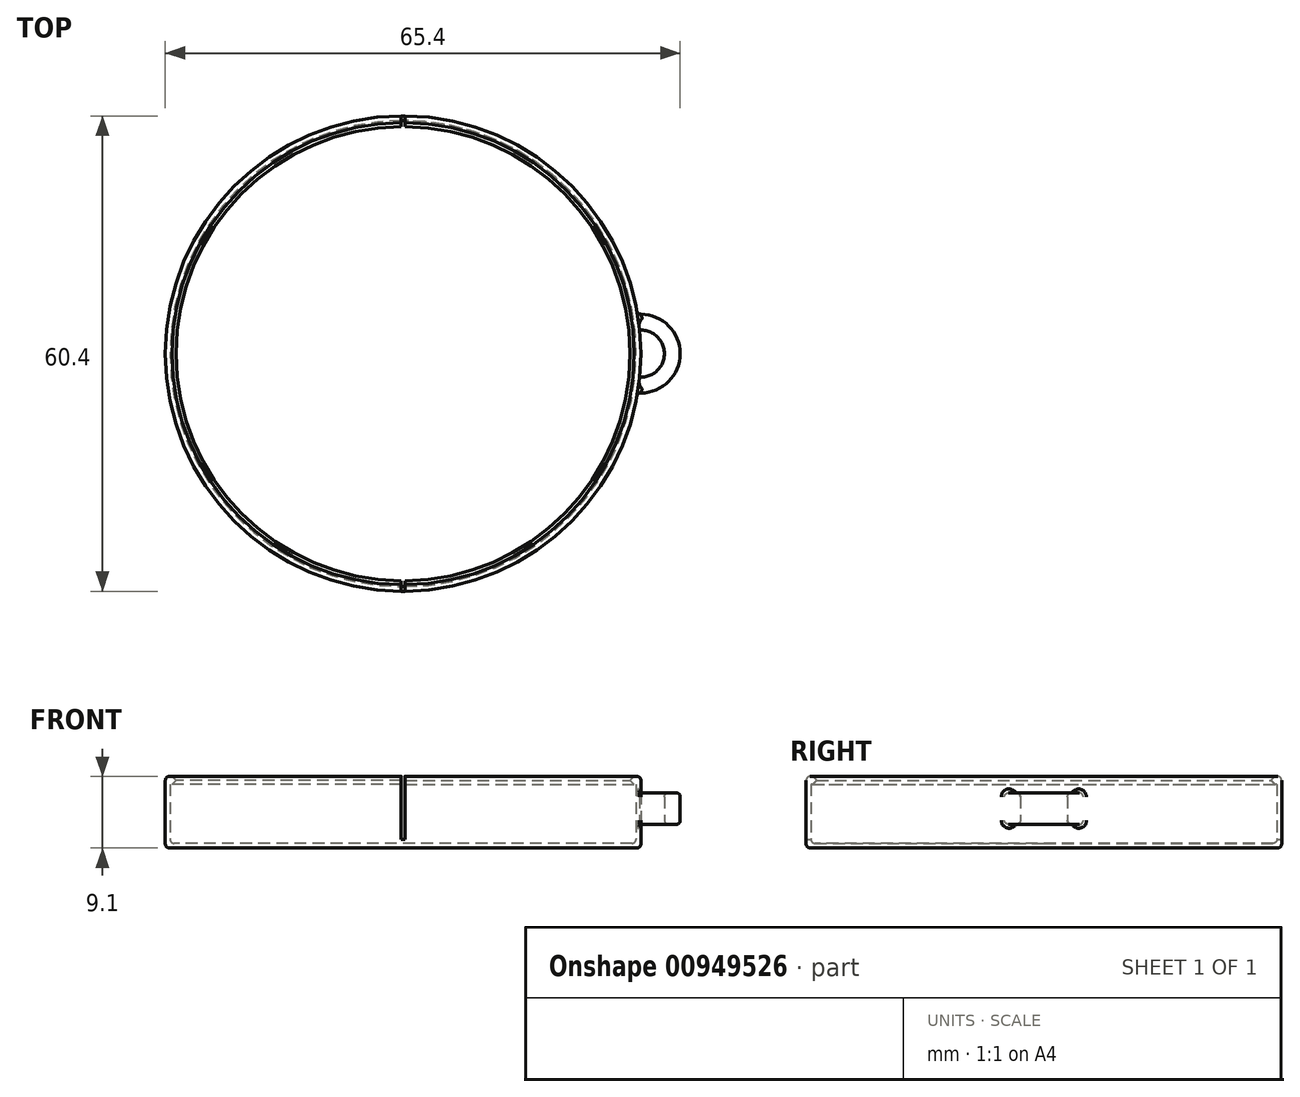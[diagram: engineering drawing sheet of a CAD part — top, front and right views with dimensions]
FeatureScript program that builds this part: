
annotation { "Feature Type Name" : "Feature", "Feature Type Description" : "" }
export const myFeature = defineFeature(function(context is Context, id is Id, definition is map)
    precondition{}
    {
        {
            var Q0;
            Q0=qCreatedBy(makeId("Top.planeOp"),FACE);
            var sketch = newSketch(context, id + "F0", { "sketchPlane" : qUnion([Q0])});
            skCircle(sketch, "E0", {"center": v(0, 0) * mm, "radius": 29.6 * mm});
            skCircle(sketch, "E1", {"center": v(0, 0) * mm, "radius": 28.85 * mm});
            skCircle(sketch, "E2.0", {"center": v(0, 0) * mm, "radius": 30.2 * mm});
            skCircle(sketch, "E3", {"center": v(30.2, 0) * mm, "radius": 3 * mm});
            skCircle(sketch, "E4", {"center": v(30.2, 0) * mm, "radius": 5 * mm});
            skSolve(sketch);
        }
        {
            var Q0;
            Q0=makeQuery(id+"F0.imprint","IMPRINT",FACE,{"disambiguationData":[TD([[makeQuery(id+"F0.imprint","IMPRINT",EDGE,{"derivedFrom":sQuery(id+"F0.wireOp",EDGE,"E0")}),-1.0]])]});
            var Q1;
            Q1=makeQuery(id+"F0.imprint","IMPRINT",FACE,{"disambiguationData":[TD([[makeQuery(id+"F0.imprint","IMPRINT",EDGE,{"derivedFrom":sQuery(id+"F0.wireOp",EDGE,"E0")}),1.0]])]});
            var Q2;
            {var subQ0=sQuery(id+"F0.wireOp",EDGE,"E4");var subQ1=sQuery(id+"F0.wireOp",EDGE,"E1");var subQ2=makeQuery(id+"F0.imprint","INTERSECT",VERTEX,{"disambiguationData":[OD(0.0)],"derivedFrom":[subQ1,subQ0]});Q2=makeQuery(id+"F0.imprint","IMPRINT",FACE,{"disambiguationData":[TD([[makeQuery(id+"F0.imprint","IMPRINT",EDGE,{"disambiguationData":[TD([[subQ2,-1.0]])],"derivedFrom":subQ1}),1.0]])]});}
            var Q3;
            {var subQ0=sQuery(id+"F0.wireOp",EDGE,"E3");var subQ1=sQuery(id+"F0.wireOp",EDGE,"E1");var subQ2=makeQuery(id+"F0.imprint","INTERSECT",VERTEX,{"disambiguationData":[OD(0.0)],"derivedFrom":[subQ1,subQ0]});Q3=makeQuery(id+"F0.imprint","IMPRINT",FACE,{"disambiguationData":[TD([[makeQuery(id+"F0.imprint","IMPRINT",EDGE,{"disambiguationData":[TD([[subQ2,1.0]])],"derivedFrom":subQ1}),1.0]])]});}
            var Q4;
            {var subQ0=sQuery(id+"F0.wireOp",EDGE,"E4");var subQ1=sQuery(id+"F0.wireOp",EDGE,"E1");var subQ2=makeQuery(id+"F0.imprint","INTERSECT",VERTEX,{"disambiguationData":[OD(0.0)],"derivedFrom":[subQ1,subQ0]});Q4=makeQuery(id+"F0.imprint","IMPRINT",FACE,{"disambiguationData":[TD([[makeQuery(id+"F0.imprint","IMPRINT",EDGE,{"disambiguationData":[TD([[subQ2,1.0]])],"derivedFrom":subQ1}),1.0]])]});}
            extrude(context, id + "F1", {"entities" : qUnion([Q0, Q1, Q2, Q3, Q4]), "depth" : 0.6 * mm, "offsetDistance" : 25 * mm});
        }
        {
            var Q0;
            Q0=makeQuery(id+"F0.imprint","IMPRINT",FACE,{"disambiguationData":[TD([[makeQuery(id+"F0.imprint","IMPRINT",EDGE,{"derivedFrom":sQuery(id+"F0.wireOp",EDGE,"E0")}),-1.0]])]});
            extrude(context, id + "F2", {"entities" : qUnion([Q0]), "operationType" : NewBodyOperationType.ADD, "depth" : 8.1 * mm, "offsetDistance" : 25 * mm});
        }
        {
            var Q0;
            Q0=makeQuery(id+"F0.imprint","IMPRINT",FACE,{"disambiguationData":[TD([[makeQuery(id+"F0.imprint","IMPRINT",EDGE,{"derivedFrom":sQuery(id+"F0.wireOp",EDGE,"E0")}),-1.0]])]});
            var Q1;
            Q1=makeQuery(id+"F0.imprint","IMPRINT",FACE,{"disambiguationData":[TD([[makeQuery(id+"F0.imprint","IMPRINT",EDGE,{"derivedFrom":sQuery(id+"F0.wireOp",EDGE,"E0")}),1.0]])]});
            extrude(context, id + "F3", {"entities" : qUnion([Q0, Q1]), "operationType" : NewBodyOperationType.ADD, "depth" : 9.1 * mm, "offsetDistance" : 25 * mm, "hasSecondDirection" : true, "secondDirectionOppositeDirection" : false, "secondDirectionDepth" : 8.1 * mm});
        }
        {
            var Q0;
            Q0=makeQuery(id+"F1.opExtrude","CAP_EDGE",EDGE,{"disambiguationData":[OSD([sQuery(id+"F0.wireOp",EDGE,"E2.0")])],"isStart":true});
            var Q1;
            Q1=makeQuery(id+"F2.boolean.opBoolean","INTERSECT",EDGE,{"derivedFrom":[makeQuery(id+"F1.opExtrude","CAP_FACE",FACE,{"disambiguationData":[OSD([sQuery(id+"F0.wireOp",EDGE,"E2.0")])],"isStart":false}),makeQuery(id+"F2.opExtrude","SWEPT_FACE",FACE,{"disambiguationData":[OSD([sQuery(id+"F0.wireOp",EDGE,"E0")])]})]});
            var Q2;
            Q2=makeQuery(id+"F3.opExtrude","CAP_EDGE",EDGE,{"disambiguationData":[OSD([sQuery(id+"F0.wireOp",EDGE,"E2.0")])],"isStart":false});
            fillet(context, id + "F4", {"entities" : qUnion([Q0, Q1, Q2]), "radius" : 0.5 * mm, "tangentPropagation" : true, "allowEdgeOverflow" : false});
        }
        {
            var Q0;
            Q0=makeQuery(id+"F3.opExtrude","CAP_EDGE",EDGE,{"disambiguationData":[OSD([sQuery(id+"F0.wireOp",EDGE,"E1")])],"isStart":true});
            var Q1;
            Q1=makeQuery(id+"F3.opExtrude","CAP_EDGE",EDGE,{"disambiguationData":[OSD([sQuery(id+"F0.wireOp",EDGE,"E1")])],"isStart":false});
            chamfer(context, id + "F5", {"entities" : qUnion([Q0, Q1]), "width" : 0.5 * mm, "tangentPropagation" : true});
        }
        {
            var Q0;
            {var subQ0=sQuery(id+"F0.wireOp",EDGE,"E4");var subQ1=sQuery(id+"F0.wireOp",EDGE,"E2.0");var subQ2=makeQuery(id+"F0.imprint","INTERSECT",VERTEX,{"disambiguationData":[OD(0.0)],"derivedFrom":[subQ1,subQ0]});Q0=makeQuery(id+"F0.imprint","IMPRINT",FACE,{"disambiguationData":[TD([[makeQuery(id+"F0.imprint","IMPRINT",EDGE,{"disambiguationData":[TD([[subQ2,1.0]])],"derivedFrom":subQ1}),-1.0]])]});}
            var Q1;
            {var subQ0=sQuery(id+"F0.wireOp",EDGE,"E4");var subQ1=sQuery(id+"F0.wireOp",EDGE,"E0");var subQ2=makeQuery(id+"F0.imprint","INTERSECT",VERTEX,{"disambiguationData":[OD(0.0)],"derivedFrom":[subQ1,subQ0]});Q1=makeQuery(id+"F0.imprint","IMPRINT",FACE,{"disambiguationData":[TD([[makeQuery(id+"F0.imprint","IMPRINT",EDGE,{"disambiguationData":[TD([[subQ2,1.0]])],"derivedFrom":subQ1}),-1.0]])]});}
            var Q2;
            {var subQ0=sQuery(id+"F0.wireOp",EDGE,"E4");var subQ1=sQuery(id+"F0.wireOp",EDGE,"E0");var subQ2=makeQuery(id+"F0.imprint","INTERSECT",VERTEX,{"disambiguationData":[OD(1.0)],"derivedFrom":[subQ1,subQ0]});Q2=makeQuery(id+"F0.imprint","IMPRINT",FACE,{"disambiguationData":[TD([[makeQuery(id+"F0.imprint","IMPRINT",EDGE,{"disambiguationData":[TD([[subQ2,-1.0]])],"derivedFrom":subQ1}),-1.0]])]});}
            extrude(context, id + "F6", {"entities" : qUnion([Q0, Q1, Q2]), "operationType" : NewBodyOperationType.ADD, "depth" : 7 * mm, "offsetDistance" : 25 * mm, "hasSecondDirection" : true, "secondDirectionOppositeDirection" : false, "secondDirectionDepth" : 3 * mm});
        }
        {
            var Q0;
            Q0=makeQuery(id+"F6.opExtrude","CAP_EDGE",EDGE,{"disambiguationData":[OSD([sQuery(id+"F0.wireOp",EDGE,"E3")])],"isStart":true});
            var Q1;
            Q1=makeQuery(id+"F6.opExtrude","CAP_EDGE",EDGE,{"disambiguationData":[OSD([sQuery(id+"F0.wireOp",EDGE,"E4")])],"isStart":true});
            var Q2;
            Q2=makeQuery(id+"F6.opExtrude","CAP_EDGE",EDGE,{"disambiguationData":[OSD([sQuery(id+"F0.wireOp",EDGE,"E3")])],"isStart":false});
            var Q3;
            Q3=makeQuery(id+"F6.opExtrude","CAP_EDGE",EDGE,{"disambiguationData":[OSD([sQuery(id+"F0.wireOp",EDGE,"E4")])],"isStart":false});
            var Q4;
            {var subQ0=sQuery(id+"F0.wireOp",EDGE,"E2.0");Q4=makeQuery(id+"F6.boolean.opBoolean","INTERSECT",EDGE,{"disambiguationData":[OD(1.0)],"derivedFrom":[makeQuery(id+"F3.boolean.opBoolean","MERGE",FACE,{"derivedFrom":[makeQuery(id+"F2.boolean.opBoolean","MERGE",FACE,{"derivedFrom":[makeQuery(id+"F1.opExtrude","SWEPT_FACE",FACE,{"disambiguationData":[OSD([subQ0])]}),makeQuery(id+"F2.opExtrude","SWEPT_FACE",FACE,{"disambiguationData":[OSD([subQ0])]})]}),makeQuery(id+"F3.opExtrude","SWEPT_FACE",FACE,{"disambiguationData":[OSD([subQ0])]})]}),makeQuery(id+"F6.opExtrude","SWEPT_FACE",FACE,{"disambiguationData":[OSD([sQuery(id+"F0.wireOp",EDGE,"E4")])]})]});}
            var Q5;
            {var subQ0=sQuery(id+"F0.wireOp",EDGE,"E2.0");Q5=makeQuery(id+"F6.boolean.opBoolean","INTERSECT",EDGE,{"disambiguationData":[OD(0.0)],"derivedFrom":[makeQuery(id+"F3.boolean.opBoolean","MERGE",FACE,{"derivedFrom":[makeQuery(id+"F2.boolean.opBoolean","MERGE",FACE,{"derivedFrom":[makeQuery(id+"F1.opExtrude","SWEPT_FACE",FACE,{"disambiguationData":[OSD([subQ0])]}),makeQuery(id+"F2.opExtrude","SWEPT_FACE",FACE,{"disambiguationData":[OSD([subQ0])]})]}),makeQuery(id+"F3.opExtrude","SWEPT_FACE",FACE,{"disambiguationData":[OSD([subQ0])]})]}),makeQuery(id+"F6.opExtrude","SWEPT_FACE",FACE,{"disambiguationData":[OSD([sQuery(id+"F0.wireOp",EDGE,"E4")])]})]});}
            fillet(context, id + "F7", {"entities" : qUnion([Q0, Q1, Q2, Q3, Q4, Q5]), "radius" : 0.5 * mm, "tangentPropagation" : true, "allowEdgeOverflow" : false});
        }
        {
            var Q0;
            Q0=qCreatedBy(makeId("Front.planeOp"),FACE);
            var sketch = newSketch(context, id + "F8", { "sketchPlane" : qUnion([Q0])});
            skLineSegment(sketch, "E5", {"start": v(0.25, 1.1) * mm, "end": v(0.25, 9.1) * mm});
            skLineSegment(sketch, "E6", {"start": v(0.25, 9.1) * mm, "end": v(0, 9.1) * mm});
            skLineSegment(sketch, "E7.MirrorCS", {"start": v(-0.25, 9.1) * mm, "end": v(0, 9.1) * mm});
            skLineSegment(sketch, "E8.MirrorCS", {"start": v(-0.25, 1.1) * mm, "end": v(-0.25, 9.1) * mm});
            skLineSegment(sketch, "E9", {"start": v(0.25, 1.1) * mm, "end": v(-0.25, 1.1) * mm});
            skSolve(sketch);
        }
        {
            var Q0;
            Q0=makeQuery(id+"F8.imprint","IMPRINT",FACE,{"disambiguationData":[TD([[makeQuery(id+"F8.imprint","IMPRINT",EDGE,{"derivedFrom":sQuery(id+"F8.wireOp",EDGE,"E5")}),1.0]])]});
            extrude(context, id + "F9", {"entities" : qUnion([Q0]), "operationType" : NewBodyOperationType.REMOVE, "endBound" : BoundingType.SYMMETRIC, "depth" : 65 * mm, "offsetDistance" : 25 * mm});
        }
    });
